# Revit family: AISC MC Shapes-Section
name_source: partatom
category: Detail Items
revit_build: Autodesk Revit Architecture 2012 (Build: 20110210_1515)
units: mm (PartAtom-declared; Revit-internal decimal feet)

## types (39) — shared parameters
Keynote = 05 12 00.G0

## per-type parameters (varying)
| type | A | W | bf | d | tf | tw | x |
| MC18X58 | 0.12 SF | 58 | 0' - 4 3/16" | 1' - 6" | 0' - 0 5/8" | 0' - 0 11/16" | 0' - 0 7/8" |
| MC18X51.9 | 0.11 SF | 51.9 | 0' - 4 3/32" | 1' - 6" | 0' - 0 5/8" | 0' - 0 19/32" | 0' - 0 27/32" |
| MC18X45.8 | 0.09 SF | 45.8 | 0' - 4" | 1' - 6" | 0' - 0 5/8" | 0' - 0 1/2" | 0' - 0 7/8" |
| MC18X42.7 | 0.09 SF | 42.7 | 0' - 3 15/16" | 1' - 6" | 0' - 0 5/8" | 0' - 0 7/16" | 0' - 0 7/8" |
| MC13X50 | 0.1 SF | 50 | 0' - 4 13/32" | 1' - 1" | 0' - 0 5/8" | 0' - 0 25/32" | 0' - 0 31/32" |
| MC13X40 | 0.08 SF | 40 | 0' - 4 3/16" | 1' - 1" | 0' - 0 5/8" | 0' - 0 9/16" | 0' - 0 31/32" |
| MC13X35 | 0.07 SF | 35 | 0' - 4 1/16" | 1' - 1" | 0' - 0 5/8" | 0' - 0 7/16" | 0' - 0 31/32" |
| MC13X31.8 | 0.06 SF | 31.8 | 0' - 4" | 1' - 1" | 0' - 0 5/8" | 0' - 0 3/8" | 0' - 1" |
| MC12X50 | 0.1 SF | 50 | 0' - 4 1/8" | 1' - 0" | 0' - 0 11/16" | 0' - 0 27/32" | 0' - 1 1/16" |
| MC12X45 | 0.09 SF | 45 | 0' - 4" | 1' - 0" | 0' - 0 11/16" | 0' - 0 23/32" | 0' - 1 1/32" |
| MC12X40 | 0.08 SF | 40 | 0' - 3 7/8" | 1' - 0" | 0' - 0 11/16" | 0' - 0 19/32" | 0' - 1 1/32" |
| MC12X35 | 0.07 SF | 35 | 0' - 3 25/32" | 1' - 0" | 0' - 0 11/16" | 0' - 0 15/32" | 0' - 1 1/16" |
| MC12X31 | 0.06 SF | 31 | 0' - 3 21/32" | 1' - 0" | 0' - 0 11/16" | 0' - 0 3/8" | 0' - 1 3/32" |
| MC12X10.6 | 0.02 SF | 10.6 | 0' - 1 1/2" | 1' - 0" | 0' - 0 5/16" | 0' - 0 3/16" | 0' - 0 9/32" |
| MC10X41.1 | 0.08 SF | 41.1 | 0' - 4 5/16" | 0' - 10" | 0' - 0 9/16" | 0' - 0 25/32" | 0' - 1 3/32" |
| MC10X33.6 | 0.07 SF | 33.6 | 0' - 4 3/32" | 0' - 10" | 0' - 0 9/16" | 0' - 0 9/16" | 0' - 1 3/32" |
| MC10X28.5 | 0.06 SF | 28.5 | 0' - 3 15/16" | 0' - 10" | 0' - 0 9/16" | 0' - 0 7/16" | 0' - 1 1/8" |
| MC10X25 | 0.05 SF | 25 | 0' - 3 13/32" | 0' - 10" | 0' - 0 9/16" | 0' - 0 3/8" | 0' - 0 15/16" |
| MC10X22 | 0.04 SF | 22 | 0' - 3 5/16" | 0' - 10" | 0' - 0 9/16" | 0' - 0 9/32" | 0' - 1" |
| MC10X8.4 | 0.02 SF | 8.4 | 0' - 1 1/2" | 0' - 10" | 0' - 0 9/32" | 0' - 0 5/32" | 0' - 0 9/32" |
| MC10X6.5 | 0.01 SF | 6.5 | 0' - 1 5/32" | 0' - 10" | 0' - 0 3/16" | 0' - 0 5/32" | 0' - 0 3/16" |
| MC9X25.4 | 0.05 SF | 25.4 | 0' - 3 1/2" | 0' - 9" | 0' - 0 9/16" | 0' - 0 7/16" | 0' - 0 31/32" |
| MC9X23.9 | 0.05 SF | 23.9 | 0' - 3 7/16" | 0' - 9" | 0' - 0 9/16" | 0' - 0 13/32" | 0' - 0 31/32" |
| MC8X22.8 | 0.05 SF | 22.8 | 0' - 3 1/2" | 0' - 8" | 0' - 0 17/32" | 0' - 0 7/16" | 0' - 1" |
| MC8X21.4 | 0.04 SF | 21.4 | 0' - 3 7/16" | 0' - 8" | 0' - 0 17/32" | 0' - 0 3/8" | 0' - 1 1/32" |
| MC8X20 | 0.04 SF | 20 | 0' - 3 1/32" | 0' - 8" | 0' - 0 1/2" | 0' - 0 13/32" | 0' - 0 27/32" |
| MC8X18.7 | 0.04 SF | 18.7 | 0' - 2 31/32" | 0' - 8" | 0' - 0 1/2" | 0' - 0 11/32" | 0' - 0 27/32" |
| MC8X8.5 | 0.02 SF | 8.5 | 0' - 1 7/8" | 0' - 8" | 0' - 0 5/16" | 0' - 0 3/16" | 0' - 0 7/16" |
| MC7X22.7 | 0.05 SF | 22.7 | 0' - 3 19/32" | 0' - 7" | 0' - 0 1/2" | 0' - 0 1/2" | 0' - 1 1/32" |
| MC7X19.1 | 0.04 SF | 19.1 | 0' - 3 7/16" | 0' - 7" | 0' - 0 1/2" | 0' - 0 11/32" | 0' - 1 3/32" |
| MC6X18 | 0.04 SF | 18 | 0' - 3 1/2" | 0' - 6" | 0' - 0 15/32" | 0' - 0 3/8" | 0' - 1 1/8" |
| MC6X15.3 | 0.03 SF | 15.3 | 0' - 3 1/2" | 0' - 6" | 0' - 0 3/8" | 0' - 0 11/32" | 0' - 1 1/16" |
| MC6X16.3 | 0.03 SF | 16.3 | 0' - 3" | 0' - 6" | 0' - 0 15/32" | 0' - 0 3/8" | 0' - 0 15/16" |
| MC6X15.1 | 0.03 SF | 15.1 | 0' - 2 15/16" | 0' - 6" | 0' - 0 15/32" | 0' - 0 5/16" | 0' - 0 15/16" |
| MC6X12 | 0.02 SF | 12 | 0' - 2 1/2" | 0' - 6" | 0' - 0 3/8" | 0' - 0 5/16" | 0' - 0 23/32" |
| MC6x7 | 0.01 SF | 7 | 0' - 1 7/8" | 0' - 6" | 0' - 0 9/32" | 0' - 0 3/16" | 0' - 0 1/2" |
| MC6x6.5 | 0.01 SF | 6.5 | 0' - 1 27/32" | 0' - 6" | 0' - 0 9/32" | 0' - 0 5/32" | 0' - 0 1/2" |
| MC4x13.8 | 0.03 SF | 13.8 | 0' - 2 1/2" | 0' - 4" | 0' - 0 1/2" | 0' - 0 1/2" | 0' - 0 27/32" |
| MC3x7.1 | 0.01 SF | 7.1 | 0' - 1 15/16" | 0' - 3" | 0' - 0 11/32" | 0' - 0 5/16" | 0' - 0 21/32" |
